# Revit family: Haworth_HarborWorkLounge_Chair_PartiallyUpholstered
name_source: partatom
category: Furniture
revit_build: Autodesk Revit 2018 (Build: 20170223_1515(x64)
units: mm (PartAtom-declared; Revit-internal decimal feet)

## family parameters
Always vertical = Yes
Cut with Voids When Loaded = No
OmniClass Number = 23.40.70.14.64.11
OmniClass Title = Office Furniture
Room Calculation Point = No
Shared = No
Work Plane-Based = No

## types (1)
- Lounge Chair
    Assembly Code = E2020200
    Base Finish = Haworth _ Paint _ Plaster
    Casters = No
    Cushion Finish = Haworth _ Fabric _ Tellure _ Ivory 3A-35
    Description = Haworth - Chair - Harbor Work Lounge - Partially Upholstered
    Glides = Yes
    Hardware Finish = Haworth _ Metal _ Brushed Aluminum
    Manufacturer = Haworth
    Model = Haworth - Chair - Harbor Work Lounge - Partially Upholstered
    No Tablet = No
    Product Page URL = https://www.haworth.com
    Revision = 2
    Shell Finish = Haworth _ Wood _ Walnut
    Size = Verify Final Dim. w/ Haworth
    Sustainability Info = http://www.haworth.com
    Table Finish = Haworth _ Wood _ Walnut
    Tablet = Yes
    Trim Finish = Haworth _ Polymer _ Black
    URL = www.haworth.com
    Warranty = http://www.haworth.com
    Wing Finish = Haworth _ Fabric _ Tellure _ Ivory 3A-35

## geometry (parser evidence)
native form markers: Sweep x9
no freeform markers — native parametric forms only
